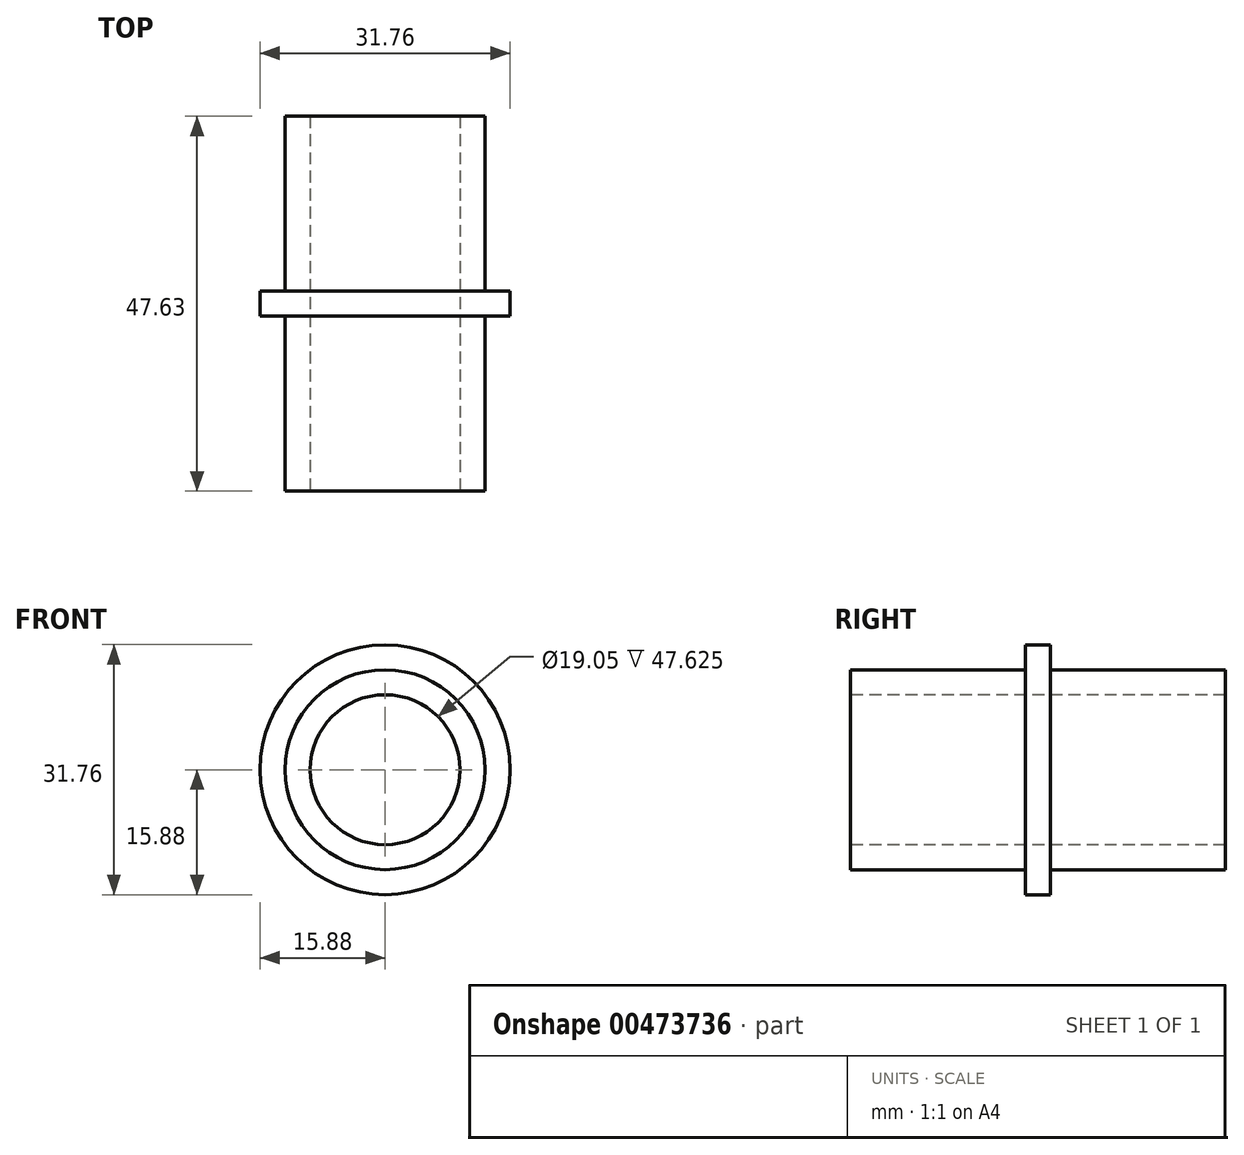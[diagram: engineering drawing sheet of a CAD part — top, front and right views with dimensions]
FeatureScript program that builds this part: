
annotation { "Feature Type Name" : "Feature", "Feature Type Description" : "" }
export const myFeature = defineFeature(function(context is Context, id is Id, definition is map)
    precondition{}
    {
        {
            var Q0;
            Q0=qCreatedBy(makeId("Front.planeOp"),FACE);
            var sketch = newSketch(context, id + "F0", { "sketchPlane" : qUnion([Q0])});
            skCircle(sketch, "E0", {"center": v(0, 0) * mm, "radius": 15.88 * mm});
            skCircle(sketch, "E1", {"center": v(0, 0) * mm, "radius": 12.7 * mm});
            skCircle(sketch, "E2", {"center": v(0, 0) * mm, "radius": 9.53 * mm});
            skSolve(sketch);
        }
        {
            var Q0;
            Q0=makeQuery(id+"F0.imprint","IMPRINT",FACE,{"disambiguationData":[TD([[makeQuery(id+"F0.imprint","IMPRINT",EDGE,{"derivedFrom":sQuery(id+"F0.wireOp",EDGE,"E0")}),1.0]])]});
            var Q1;
            Q1=makeQuery(id+"F0.imprint","IMPRINT",FACE,{"disambiguationData":[TD([[makeQuery(id+"F0.imprint","IMPRINT",EDGE,{"derivedFrom":sQuery(id+"F0.wireOp",EDGE,"E1")}),1.0]])]});
            extrude(context, id + "F1", {"entities" : qUnion([Q0, Q1]), "oppositeDirection" : true, "depth" : 3.17 * mm});
        }
        {
            var Q0;
            Q0=makeQuery(id+"F0.imprint","IMPRINT",FACE,{"disambiguationData":[TD([[makeQuery(id+"F0.imprint","IMPRINT",EDGE,{"derivedFrom":sQuery(id+"F0.wireOp",EDGE,"E1")}),1.0]])]});
            extrude(context, id + "F2", {"entities" : qUnion([Q0]), "operationType" : NewBodyOperationType.ADD, "oppositeDirection" : true, "depth" : 25.4 * mm});
        }
        {
            var Q0;
            Q0=makeQuery(id+"F0.imprint","IMPRINT",FACE,{"disambiguationData":[TD([[makeQuery(id+"F0.imprint","IMPRINT",EDGE,{"derivedFrom":sQuery(id+"F0.wireOp",EDGE,"E1")}),1.0]])]});
            extrude(context, id + "F3", {"entities" : qUnion([Q0]), "operationType" : NewBodyOperationType.ADD, "depth" : 22.22 * mm});
        }
    });
